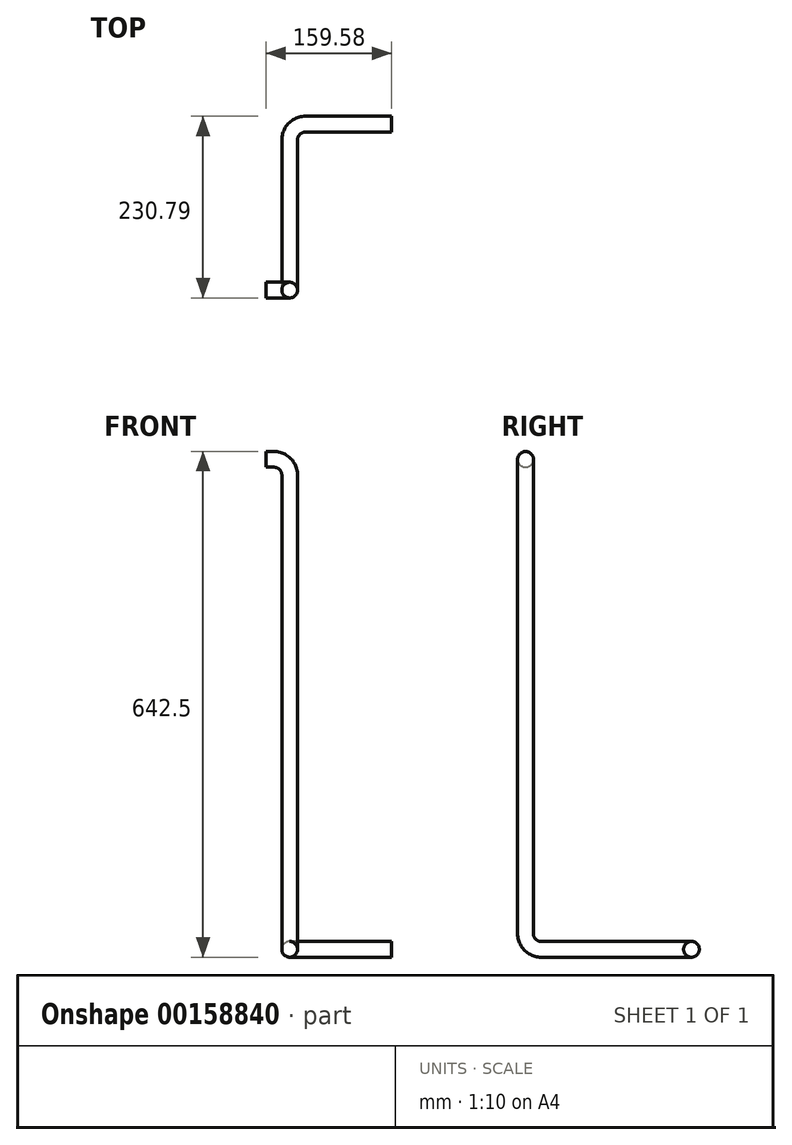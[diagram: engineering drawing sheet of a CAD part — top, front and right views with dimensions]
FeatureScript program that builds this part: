
annotation { "Feature Type Name" : "Feature", "Feature Type Description" : "" }
export const myFeature = defineFeature(function(context is Context, id is Id, definition is map)
    precondition{}
    {
        {
            var Q0;
            Q0=qCreatedBy(makeId("Front.planeOp"),FACE);
            var sketch = newSketch(context, id + "F0", { "sketchPlane" : qUnion([Q0])});
            skLineSegment(sketch, "E0", {"start": v(0, 0) * mm, "end": v(10, 0) * mm});
            skLineSegment(sketch, "E1", {"start": v(30, -20) * mm, "end": v(30, -602.5) * mm});
            skPoint(sketch, "E2.visualSharp", {"position": v(30, 0) * mm});
            skArc(sketch, "E2.filletArc", {"start": v(30, -20) * mm, "mid": v(24.14, -5.86) * mm, "end": v(10, 0) * mm});
            skSolve(sketch);
        }
        {
            var Q0;
            Q0=qCreatedBy(makeId("Top.planeOp"),FACE);
            cPlane(context, id + "F1", {"entities" : qUnion([Q0]), "cplaneType" : CPlaneType.OFFSET, "offset" : 622.5 * mm, "oppositeDirection" : true, "width" : 150 * mm, "height" : 150 * mm});
        }
        {
            var Q0;
            Q0=qCreatedBy(id+"F1.planeOp",FACE);
            var sketch = newSketch(context, id + "F2", { "sketchPlane" : qUnion([Q0])});
            skPoint(sketch, "E3.visualSharp", {"position": v(30, 210.78) * mm});
            skLineSegment(sketch, "E4", {"start": v(30, 190.79) * mm, "end": v(30, 20) * mm});
            skLineSegment(sketch, "E5", {"start": v(50, 210.78) * mm, "end": v(159.58, 210.79) * mm});
            skArc(sketch, "E6.filletArc", {"start": v(50, 210.79) * mm, "mid": v(35.86, 204.93) * mm, "end": v(30, 190.79) * mm});
            skSolve(sketch);
        }
        {
            var Q0;
            Q0=qCreatedBy(makeId("Right.planeOp"),FACE);
            cPlane(context, id + "F3", {"entities" : qUnion([Q0]), "cplaneType" : CPlaneType.OFFSET, "offset" : 30 * mm, "width" : 150 * mm, "height" : 150 * mm});
        }
        {
            var Q0;
            Q0=qCreatedBy(id+"F3.planeOp",FACE);
            var sketch = newSketch(context, id + "F4", { "sketchPlane" : qUnion([Q0])});
            skLineSegment(sketch, "E7", {"start": v(0, -503.6) * mm, "end": v(0, -602.5) * mm});
            skPoint(sketch, "E8.visualSharp", {"position": v(0, -622.5) * mm});
            skArc(sketch, "E8.filletArc", {"start": v(0, -602.5) * mm, "mid": v(5.86, -616.64) * mm, "end": v(20, -622.5) * mm});
            skSolve(sketch);
        }
        {
            var Q0;
            Q0=qCreatedBy(makeId("Right.planeOp"),FACE);
            var sketch = newSketch(context, id + "F5", { "sketchPlane" : qUnion([Q0])});
            skCircle(sketch, "E9", {"center": v(0, 0) * mm, "radius": 10 * mm});
            skSolve(sketch);
        }
        {
            var Q0;
            Q0=makeQuery(id+"F5.imprint","IMPRINT",FACE,{"disambiguationData":[TD([[makeQuery(id+"F5.imprint","IMPRINT",EDGE,{"derivedFrom":sQuery(id+"F5.wireOp",EDGE,"E9")}),1.0]])]});
            var Q1;
            Q1=sQuery(id+"F0.wireOp",EDGE,"E0");
            var Q2;
            Q2=sQuery(id+"F0.wireOp",EDGE,"E2.filletArc");
            var Q3;
            Q3=sQuery(id+"F0.wireOp",EDGE,"E1");
            var Q4;
            Q4=sQuery(id+"F4.wireOp",EDGE,"E8.filletArc");
            var Q5;
            Q5=sQuery(id+"F2.wireOp",EDGE,"E4");
            var Q6;
            Q6=sQuery(id+"F2.wireOp",EDGE,"E6.filletArc");
            var Q7;
            Q7=sQuery(id+"F2.wireOp",EDGE,"E5");
            sweep(context, id + "F6", {"profiles" : qUnion([Q0]), "path" : qUnion([Q1, Q2, Q3, Q4, Q5, Q6, Q7])});
        }
    });
